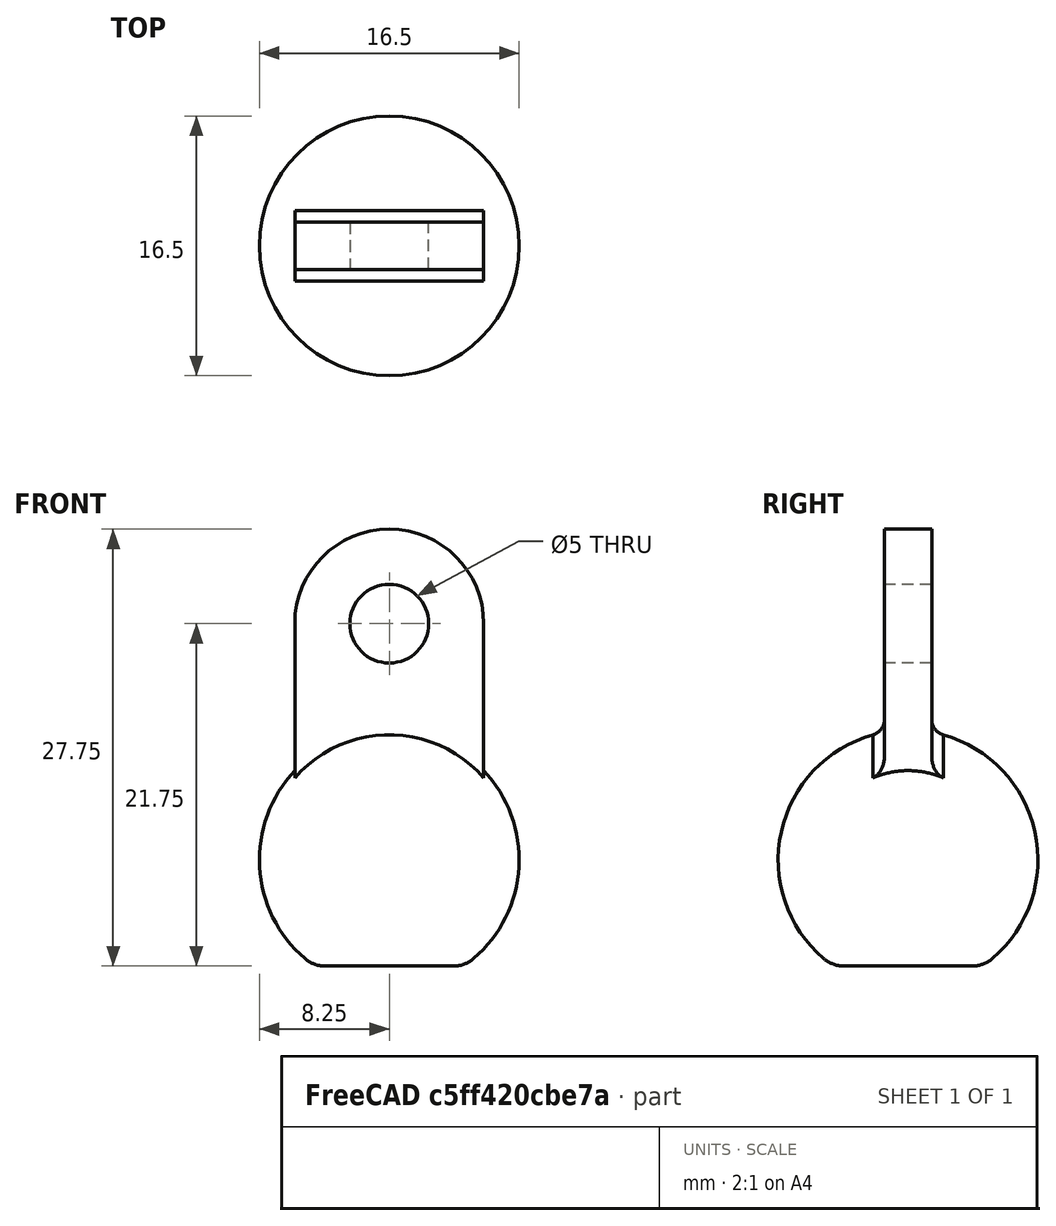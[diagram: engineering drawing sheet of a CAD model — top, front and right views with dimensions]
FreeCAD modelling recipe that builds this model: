
FCSTD DOCUMENT  (FreeCAD 2023.114R26244 +5346 (Git))
Label: ball
License: All rights reserved
LicenseURL: http://en.wikipedia.org/wiki/All_rights_reserved
objects: Sketcher::SketchObject×5, PartDesign::Pad×2, PartDesign::Pocket×2, PartDesign::Fillet×2, App::MeasureDistance×2, Spreadsheet::Sheet×1, PartDesign::Revolution×1, PartDesign::Body×1, Mesh::Feature×1
note: 32 computed .brp shape members not serialized (recipe doc carries the construction recipe); baked Part::Feature solids carry a one-line shape summary decoded from their .brp

FEATURE [Spreadsheet::Sheet] Spreadsheet
  PythonMode = false
  ShowCells = 0
  TreeRank = 1
  cells = A1=ball_dia; B1(ball_dia)=16.5; A2=ball_flatspot; B2(ball_flatspot)=1.5; A3=clevis_thk; B3(clevis_thk)=3; A4=clevis_dia; B4(clevis_dia)=12; A5=clevis_center; B5(clevis_center)=15; A6=clevis_hole_dia; B6(clevis_hole_dia)=5
FEATURE [Sketcher::SketchObject] Sketch
  ArcFitTolerance = 1e-06
  AttachmentSupport = -> [XZ_Plane]
  ExternalBSplineMaxDegree = 5
  ExternalBSplineTolerance = 0.0001
  FullyConstrained = true
  InternalTolerance = 1e-06
  InvalidShape = false
  MakeInternals = false
  MapMode = 5
  Placement = pos=(0,0,0) rot=(1,0,0;1.5708rad)
  Support = -> [XZ_Plane]
  TreeRank = 12
  ValidateShape = true
  expr: Constraints[5] = Spreadsheet.ball_dia
  expr: Constraints[6] = Spreadsheet.ball_dia / 2 - Spreadsheet.ball_flatspot
  sketch-geometry (2):
    g0: ArcOfCircle CenterX=0 CenterY=6.75 CenterZ=0 NormalX=0 NormalY=0 NormalZ=1 AngleXU=0 Radius=8.25 StartAngle=4.71239 EndAngle=7.85398
    g1: LineSegment StartX=0 StartY=15 StartZ=0 EndX=0 EndY=-1.5 EndZ=0
  constraints (7):
    c: PointOnObject(g0,g-2)
    c: PointOnObject(g0,g-2)
    c: Coincident(g1,g0)
    c: Coincident(g1,g0)
    c: Vertical(g1)
    c: Diameter(g0) = 16.5
    c: Distance(g-1,g0) = 6.75
FEATURE [PartDesign::Revolution] Revolution
  AddSubType = 0
  Angle = 360
  Axis = (-3e-16,3e-16,1)
  Base = (0,0,0)
  ClaimChildren = false
  Fit = 0
  FitJoin = 0
  InnerFit = 0
  InnerFitJoin = 0
  InvalidShape = false
  Linearize = true
  NewSolid = false
  Profile = -> Sketch
  ReferenceAxis = -> Z_Axis
  Refine = true
  Suppress = false
  TreeRank = 13
  ValidateShape = true
  _ProfileBasedVersion = 1
FEATURE [Sketcher::SketchObject] Sketch001
  ArcFitTolerance = 1e-06
  AttachmentSupport = -> [Sketch]
  ExternalBSplineMaxDegree = 5
  ExternalBSplineTolerance = 0.0001
  ExternalGeometry = -> [Sketch]
  FullyConstrained = true
  InternalTolerance = 1e-06
  InvalidShape = false
  MakeInternals = false
  MapMode = 5
  Placement = pos=(0,0,0) rot=(1,0,0;1.5708rad)
  Support = -> [Sketch]
  TreeRank = 14
  ValidateShape = true
  expr: Constraints[1] = Spreadsheet.clevis_dia
  expr: Constraints[2] = Spreadsheet.clevis_center
  sketch-geometry (1):
    g0: Circle CenterX=0 CenterY=21.75 CenterZ=0 NormalX=0 NormalY=0 NormalZ=1 AngleXU=0 Radius=6
  constraints (3):
    c: PointOnObject(g0,g-2)
    c: Diameter(g0) = 12
    c: Distance(g-3,g0) = 15
FEATURE [PartDesign::Pad] Pad
  AddSubType = 0
  AlongSketchNormal = false
  AutoTaperInnerAngle = true
  BaseFeature = -> Revolution
  CheckUpToFaceLimits = true
  ClaimChildren = false
  Direction = (0,-1,-2e-16)
  Fit = 0
  FitJoin = 0
  InnerFit = 0
  InnerFitJoin = 0
  InvalidShape = false
  Length = 3
  Length2 = 100
  Linearize = true
  Midplane = true
  NewSolid = false
  Profile = -> Sketch001
  Refine = true
  Suppress = false
  TaperInnerAngle = 0
  TaperInnerAngleRev = 0
  TreeRank = 15
  Type = 0
  ValidateShape = true
  _ProfileBasedVersion = 1
  expr: Length = Spreadsheet.clevis_thk
FEATURE [Sketcher::SketchObject] Sketch002
  ArcFitTolerance = 1e-06
  AttachmentSupport = -> [XZ_Plane]
  ExternalBSplineMaxDegree = 5
  ExternalBSplineTolerance = 0.0001
  ExternalGeometry = -> [Pad]
  FullyConstrained = true
  InternalTolerance = 1e-06
  InvalidShape = false
  MakeInternals = false
  MapMode = 5
  Placement = pos=(0,0,0) rot=(1,0,0;1.5708rad)
  Support = -> [XZ_Plane]
  TreeRank = 16
  ValidateShape = true
  sketch-geometry (4):
    g0: LineSegment StartX=-6 StartY=21.75 StartZ=0 EndX=6 EndY=21.75 EndZ=0
    g1: LineSegment StartX=6 StartY=21.75 StartZ=0 EndX=6 EndY=6.75 EndZ=0
    g2: LineSegment StartX=6 StartY=6.75 StartZ=0 EndX=-6 EndY=6.75 EndZ=0
    g3: LineSegment StartX=-6 StartY=6.75 StartZ=0 EndX=-6 EndY=21.75 EndZ=0
  constraints (12):
    c: Coincident(g0,g1)
    c: Coincident(g1,g2)
    c: Coincident(g2,g3)
    c: Coincident(g3,g0)
    c: Horizontal(g0)
    c: Horizontal(g2)
    c: Vertical(g1)
    c: Vertical(g3)
    c: PointOnObject(g0,g-3)
    c: PointOnObject(g-3,g0)
    c: PointOnObject(g-4,g2)
    c: PointOnObject(g0,g-3)
FEATURE [PartDesign::Pad] Pad001
  AddSubType = 0
  AlongSketchNormal = false
  AutoTaperInnerAngle = true
  BaseFeature = -> Pad
  CheckUpToFaceLimits = true
  ClaimChildren = false
  Direction = (0,-1,-2e-16)
  Fit = 0
  FitJoin = 0
  InnerFit = 0
  InnerFitJoin = 0
  InvalidShape = false
  Length = 3
  Length2 = 100
  Linearize = true
  Midplane = true
  NewSolid = false
  Profile = -> Sketch002
  Refine = true
  Suppress = false
  TaperInnerAngle = 0
  TaperInnerAngleRev = 0
  TreeRank = 17
  Type = 0
  ValidateShape = true
  _ProfileBasedVersion = 1
  expr: Length = Spreadsheet.clevis_thk
FEATURE [Sketcher::SketchObject] Sketch003
  ArcFitTolerance = 1e-06
  AttachmentSupport = -> [XZ_Plane]
  ExternalBSplineMaxDegree = 5
  ExternalBSplineTolerance = 0.0001
  ExternalGeometry = -> [Pad001]
  FullyConstrained = true
  InternalTolerance = 1e-06
  InvalidShape = false
  MakeInternals = false
  MapMode = 5
  Placement = pos=(0,0,0) rot=(1,0,0;1.5708rad)
  Support = -> [XZ_Plane]
  TreeRank = 18
  ValidateShape = true
  expr: Constraints[1] = Spreadsheet.clevis_hole_dia
  sketch-geometry (1):
    g0: Circle CenterX=0 CenterY=21.75 CenterZ=0 NormalX=0 NormalY=0 NormalZ=1 AngleXU=0 Radius=2.5
  constraints (2):
    c: Coincident(g0,g-3)
    c: Diameter(g0) = 5
FEATURE [PartDesign::Pocket] Pocket
  AddSubType = 1
  AutoTaperInnerAngle = true
  BaseFeature = -> Pad001
  CheckUpToFaceLimits = true
  ClaimChildren = false
  Fit = 0
  FitJoin = 0
  InnerFit = 0
  InnerFitJoin = 0
  InvalidShape = false
  Length = 5
  Length2 = 100
  Linearize = true
  Midplane = true
  NewSolid = false
  Profile = -> Sketch003
  Refine = true
  Suppress = false
  TaperInnerAngle = 0
  TaperInnerAngleRev = 0
  TreeRank = 19
  Type = 1
  ValidateShape = true
  _ProfileBasedVersion = 1
  _Version = 1
FEATURE [PartDesign::Fillet] Fillet
  AddSubType = 0
  Base = -> Pocket [Edge5,Edge3]
  BaseFeature = -> Pocket
  InvalidShape = false
  NewSolid = false
  Radius = 1
  Refine = true
  SupportTransform = false
  Suppress = false
  TreeRank = 20
  ValidateShape = true
FEATURE [Sketcher::SketchObject] Sketch004
  ArcFitTolerance = 1e-06
  AttachmentSupport = -> [Sketch]
  ExternalBSplineMaxDegree = 5
  ExternalBSplineTolerance = 0.0001
  FullyConstrained = false
  InternalTolerance = 1e-06
  InvalidShape = false
  MakeInternals = false
  MapMode = 5
  Placement = pos=(0,0,0) rot=(1,0,0;1.5708rad)
  Support = -> [Sketch]
  TreeRank = 21
  ValidateShape = true
  sketch-geometry (4):
    g0: LineSegment StartX=-11.6754 StartY=0 StartZ=0 EndX=11.6754 EndY=0 EndZ=0
    g1: LineSegment StartX=11.6754 StartY=0 StartZ=0 EndX=11.6754 EndY=-6.06258 EndZ=0
    g2: LineSegment StartX=11.6754 StartY=-6.06258 StartZ=0 EndX=-11.6754 EndY=-6.06258 EndZ=0
    g3: LineSegment StartX=-11.6754 StartY=-6.06258 StartZ=0 EndX=-11.6754 EndY=0 EndZ=0
  constraints (9):
    c: Coincident(g0,g1)
    c: Coincident(g1,g2)
    c: Coincident(g2,g3)
    c: Coincident(g3,g0)
    c: Horizontal(g2)
    c: Vertical(g1)
    c: Vertical(g3)
    c: PointOnObject(g0,g-1)
    c: Symmetric(g0,g0,g-2)
FEATURE [PartDesign::Pocket] Pocket001
  AddSubType = 1
  AutoTaperInnerAngle = true
  BaseFeature = -> Fillet
  CheckUpToFaceLimits = true
  ClaimChildren = false
  Fit = 0
  FitJoin = 0
  InnerFit = 0
  InnerFitJoin = 0
  InvalidShape = false
  Length = 5
  Length2 = 100
  Linearize = true
  Midplane = true
  NewSolid = false
  Profile = -> Sketch004
  Refine = true
  Suppress = false
  TaperInnerAngle = 0
  TaperInnerAngleRev = 0
  TreeRank = 22
  Type = 1
  ValidateShape = true
  _ProfileBasedVersion = 1
  _Version = 1
FEATURE [PartDesign::Fillet] Fillet001
  AddSubType = 0
  Base = -> Pocket001 [Edge6]
  BaseFeature = -> Pocket001
  InvalidShape = false
  NewSolid = false
  Radius = 2
  Refine = true
  SupportTransform = false
  Suppress = false
  TreeRank = 23
  ValidateShape = true
FEATURE [PartDesign::Body] Body
  AutoGroupSolids = false
  ClaimAllChildren = false
  ExportMode = 0
  Group = -> [Sketch,Revolution,Sketch001,Pad,Sketch002,Pad001,Sketch003,Pocket,Fillet,Sketch004,Pocket001,Fillet001]
  InvalidShape = false
  Origin = -> Origin
  Tip = -> Fillet001
  TreeRank = 11
  ValidateShape = true
  _ExportChildren = -> [Revolution,Pad,Pad001,Pocket,Fillet,Pocket001,Fillet001]
  _GroupVersion = 1
FEATURE [App::MeasureDistance] Distance  label="Distance: 9.16 mm"
  Distance = 9.15846
  P1 = (3.90182,2.3986,-6e-16)
  P2 = (-4.01837,-2.2001,6e-16)
  TreeRank = 24
FEATURE [App::MeasureDistance] Distance001  label="Distance: 8.12 mm"
  Distance = 8.12284
  P1 = (-3.63981,-1.80327,-3e-16)
  P2 = (3.57579,1.9271,4e-16)
  TreeRank = 25
FEATURE [Mesh::Feature] Mesh  label="Body (Meshed)"
  TreeRank = 26
